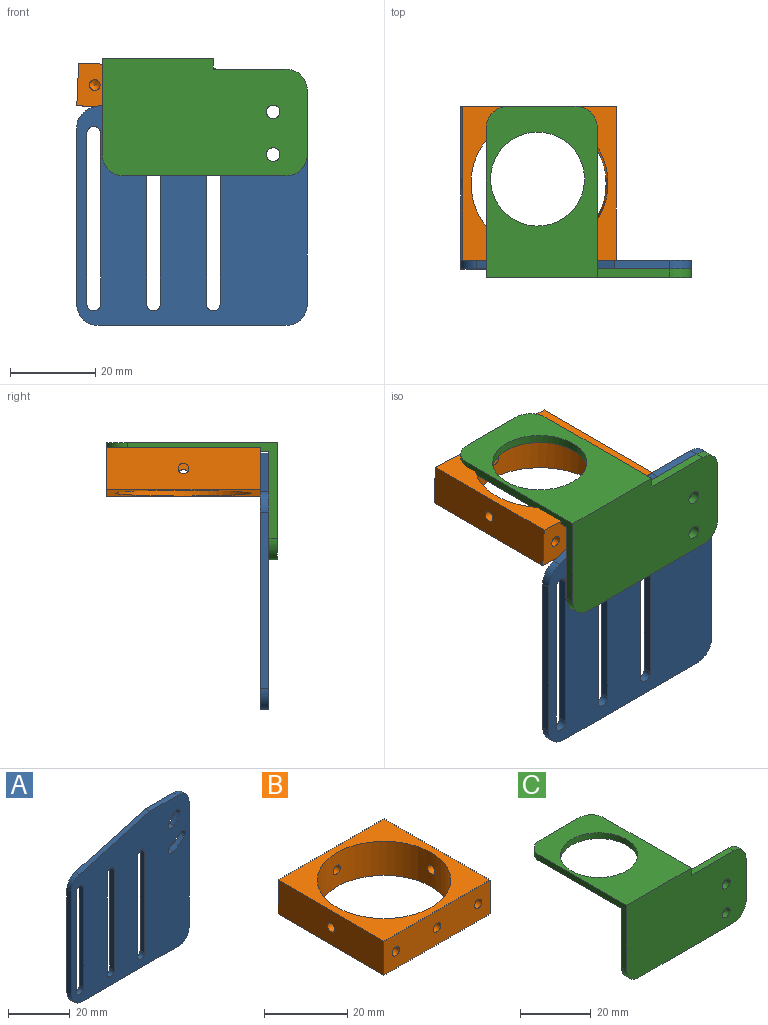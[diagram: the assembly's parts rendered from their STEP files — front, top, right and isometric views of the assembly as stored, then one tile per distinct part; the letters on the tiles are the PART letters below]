
ASSEMBLY  parts=3 mates=1
PART A: 31 faces, bbox 54x2x60 mm
  f0: plane 40x2mm, normal (1,0,0), area 80mm2, adj f1,f24,f25,f26
  f1: cylinder r=1.6mm len=3.2mm, axis (0,1,0), area 10.1mm2, adj f0,f2,f25,f26
  f2: plane 40x2mm, normal (-1,0,0), area 80mm2, adj f1,f24,f25,f26
  f3: cylinder r=1.6mm len=3.2mm, axis (0,1,0), area 10.1mm2, adj f4,f19,f25,f26
  f4: plane 40x2mm, normal (-1,0,0), area 80mm2, adj f3,f5,f25,f26
  f5: cylinder r=1.6mm len=3.2mm, axis (0,1,0), area 10.1mm2, adj f4,f19,f25,f26
  f6: plane 50x2mm, normal (1,0,0), area 100mm2, adj f25,f26,f27,f30
  f7: plane 13x2mm, normal (0,0,1), area 26mm2, adj f8,f25,f26,f27
  f8: plane 32.34x8.98mm, normal (-0.27,0,0.96), area 67.1mm2, adj f7,f25,f26,f28
  f9: plane 41.2x2mm, normal (-1,0,0), area 82.4mm2, adj f25,f26,f28,f29
  f10: plane 40x2mm, normal (1,0,0), area 80mm2, adj f11,f21,f25,f26
  f11: cylinder r=1.6mm len=3.2mm, axis (0,1,0), area 10.1mm2, adj f10,f12,f25,f26
  f12: plane 40x2mm, normal (-1,0,0), area 80mm2, adj f11,f21,f25,f26
  f13: cylinder r=1.6mm len=2.73mm, axis (0,1,0), area 10.1mm2, adj f14,f22,f25,f26
  f14: cylinder r=12.54mm len=2.6mm, axis (0,1,0), area 6.6mm2, adj f13,f15,f25,f26
  f15: cylinder r=1.6mm len=2.99mm, axis (0,1,0), area 10.1mm2, adj f14,f22,f25,f26
  f16: cylinder r=1.6mm len=3.03mm, axis (0,1,0), area 10.1mm2, adj f17,f23,f25,f26
  f17: cylinder r=20.76mm len=4.49mm, axis (0,1,0), area 10.9mm2, adj f16,f18,f25,f26
  f18: cylinder r=1.6mm len=2.8mm, axis (0,1,0), area 10.1mm2, adj f17,f23,f25,f26
  f19: plane 40x2mm, normal (1,0,0), area 80mm2, adj f3,f5,f25,f26
  f20: plane 44x2mm, normal (0,0,-1), area 88mm2, adj f25,f26,f29,f30
  f21: cylinder r=1.6mm len=3.2mm, axis (0,1,0), area 10.1mm2, adj f10,f12,f25,f26
  f22: cylinder r=15.74mm len=3.26mm, axis (0,1,0), area 8.2mm2, adj f13,f15,f25,f26
  f23: cylinder r=23.96mm len=5.18mm, axis (0,1,0), area 12.5mm2, adj f16,f18,f25,f26
  f24: cylinder r=1.6mm len=3.2mm, axis (0,1,0), area 10.1mm2, adj f0,f2,f25,f26
  f25: plane 60x54mm, normal (0,-1,0), area 2586.4mm2, adj f0,f1,f2,f3,f4,f5,f6,f7
  f26: plane 60x54mm, normal (0,1,0), area 2586.4mm2, adj f0,f1,f2,f3,f4,f5,f6,f7
  f27: cylinder r=5mm len=5mm, axis (0,1,0), area 15.7mm2, adj f6,f7,f25,f26
  f28: cylinder r=5mm len=4.82mm, axis (0,1,0), area 13mm2, adj f8,f9,f25,f26
  f29: cylinder r=5mm len=5mm, axis (0,1,0), area 15.7mm2, adj f9,f20,f25,f26
  f30: cylinder r=5mm len=5mm, axis (0,-1,0), area 15.7mm2, adj f6,f20,f25,f26
PART B: 15 faces, bbox 36x36x10 mm
  f0: cylinder r=16.05mm len=32.1mm, axis (0,0,1), area 988.8mm2, adj f5,f6,f7,f8,f9,f10
  f1: plane 36x10mm, normal (0,1,0), area 355.1mm2, adj f2,f4,f5,f6,f7
  f2: plane 36x10mm, normal (-1,0,0), area 355.1mm2, adj f1,f3,f5,f6,f10
  f3: plane 36x10mm, normal (0,-1,0), area 345.3mm2, adj f2,f4,f5,f6,f8,f12,f14
  f4: plane 36x10mm, normal (1,0,0), area 355.1mm2, adj f1,f3,f5,f6,f9
  f5: plane 36x36mm, normal (0,0,-1), area 486.7mm2, adj f0,f1,f2,f3,f4
  f6: plane 36x36mm, normal (0,0,1), area 486.7mm2, adj f0,f1,f2,f3,f4
  f7: cylinder r=1.25mm len=2.5mm, axis (0,1,0), area 15.5mm2, adj f0,f1
  f8: cylinder r=1.25mm len=2.5mm, axis (0,1,0), area 15.5mm2, adj f0,f3
  f9: cylinder r=1.25mm len=2.5mm, axis (-1,0,0), area 15.5mm2, adj f0,f4
  f10: cylinder r=1.25mm len=2.5mm, axis (-1,0,0), area 15.5mm2, adj f0,f2
  f11: cone r=0mm half-angle=59deg, axis (0,-1,0), area 5.7mm2, adj f12
  f12: cylinder r=1.25mm len=6mm, axis (0,-1,0), area 47.1mm2, adj f3,f11
  f13: cone r=0mm half-angle=59deg, axis (0,-1,0), area 5.7mm2, adj f14
  f14: cylinder r=1.25mm len=6mm, axis (0,-1,0), area 47.1mm2, adj f3,f13
PART C: 29 faces, bbox 48x40x27.5 mm
  f0: plane 15x2mm, normal (1,0,0), area 30mm2, adj f1,f2,f24,f27
  f1: plane 48x25.5mm, normal (0,1,0), area 1176.8mm2, adj f0,f3,f4,f6,f9,f10,f11,f12
  f2: plane 48x27.5mm, normal (0,-1,0), area 1232.8mm2, adj f0,f3,f4,f5,f6,f10,f11,f12
  f3: plane 35x22.5mm, normal (-1,0,0), area 111mm2, adj f1,f2,f5,f9,f26,f28
  f4: plane 38x2mm, normal (0,0,-1), area 76mm2, adj f1,f2,f27,f28
  f5: plane 40x26mm, normal (0,0,1), area 649.1mm2, adj f2,f3,f6,f7,f8,f25,f26
  f6: plane 35x2.5mm, normal (1,0,0), area 71mm2, adj f1,f2,f5,f9,f12,f25
  f7: cylinder r=11mm len=22mm, axis (0,0,1), area 138.2mm2, adj f5,f9
  f8: plane 16x6mm, normal (0,1,0), area 48mm2, adj f5,f9,f19,f20,f23,f25,f26
  f9: plane 38x26mm, normal (0,0,-1), area 590.6mm2, adj f1,f3,f6,f7,f8,f18,f19,f20
  f10: cylinder r=1.6mm len=3.2mm, axis (0,-1,0), area 20.1mm2, adj f1,f2
  f11: cylinder r=1.6mm len=3.2mm, axis (0,-1,0), area 20.1mm2, adj f1,f2
  f12: plane 17x2mm, normal (0,0,1), area 34mm2, adj f1,f2,f6,f24
  f13: plane 2x2mm, normal (0,0,1), area 4mm2, adj f1,f14,f16,f17
  f14: plane 2x2mm, normal (1,0,0), area 4mm2, adj f1,f13,f15,f17
  f15: plane 2x2mm, normal (0,0,-1), area 4mm2, adj f1,f14,f16,f17
  f16: plane 2x2mm, normal (-1,0,0), area 4mm2, adj f1,f13,f15,f17
  f17: plane 2x2mm, normal (0,1,0), area 4mm2, adj f13,f14,f15,f16
  f18: plane 4x1.75mm, normal (0,-1,0), area 7mm2, adj f9,f19,f22,f23
  f19: plane 4x1.6mm, normal (-1,0,0), area 6.4mm2, adj f8,f9,f18,f23
  f20: plane 4x1.6mm, normal (1,0,0), area 6.4mm2, adj f8,f9,f21,f23
  f21: plane 4x1.75mm, normal (0,-1,0), area 7mm2, adj f9,f20,f22,f23
  f22: extruded ~4x0.5mm, area 4.4mm2, adj f9,f18,f21,f23
  f23: plane 4x2.24mm, normal (0,0,-1), area 6.6mm2, adj f8,f18,f19,f20,f21,f22
  f24: cylinder r=5mm len=5mm, axis (0,-1,0), area 15.7mm2, adj f0,f1,f2,f12
  f25: cylinder r=5mm len=5mm, axis (0,0,1), area 15.7mm2, adj f5,f6,f8,f9
  f26: cylinder r=5mm len=5mm, axis (0,0,1), area 15.7mm2, adj f3,f5,f8,f9
  f27: cylinder r=5mm len=5mm, axis (0,-1,0), area 15.7mm2, adj f0,f1,f2,f4
  f28: cylinder r=5mm len=5mm, axis (0,1,0), area 15.7mm2, adj f1,f2,f3,f4
PLACE A t=(-7.89,-3.58,-3.03)mm
PLACE B rot(axis=(0,1,0),2.5deg) t=(-7.45,-3.58,-2.38)mm
PLACE C t=(-7.89,-2.58,-2.53)mm
MATE slider C.f10 <-> A.f13  axis (0,1,0) through (20.11,-23.58,-13.03)mm
